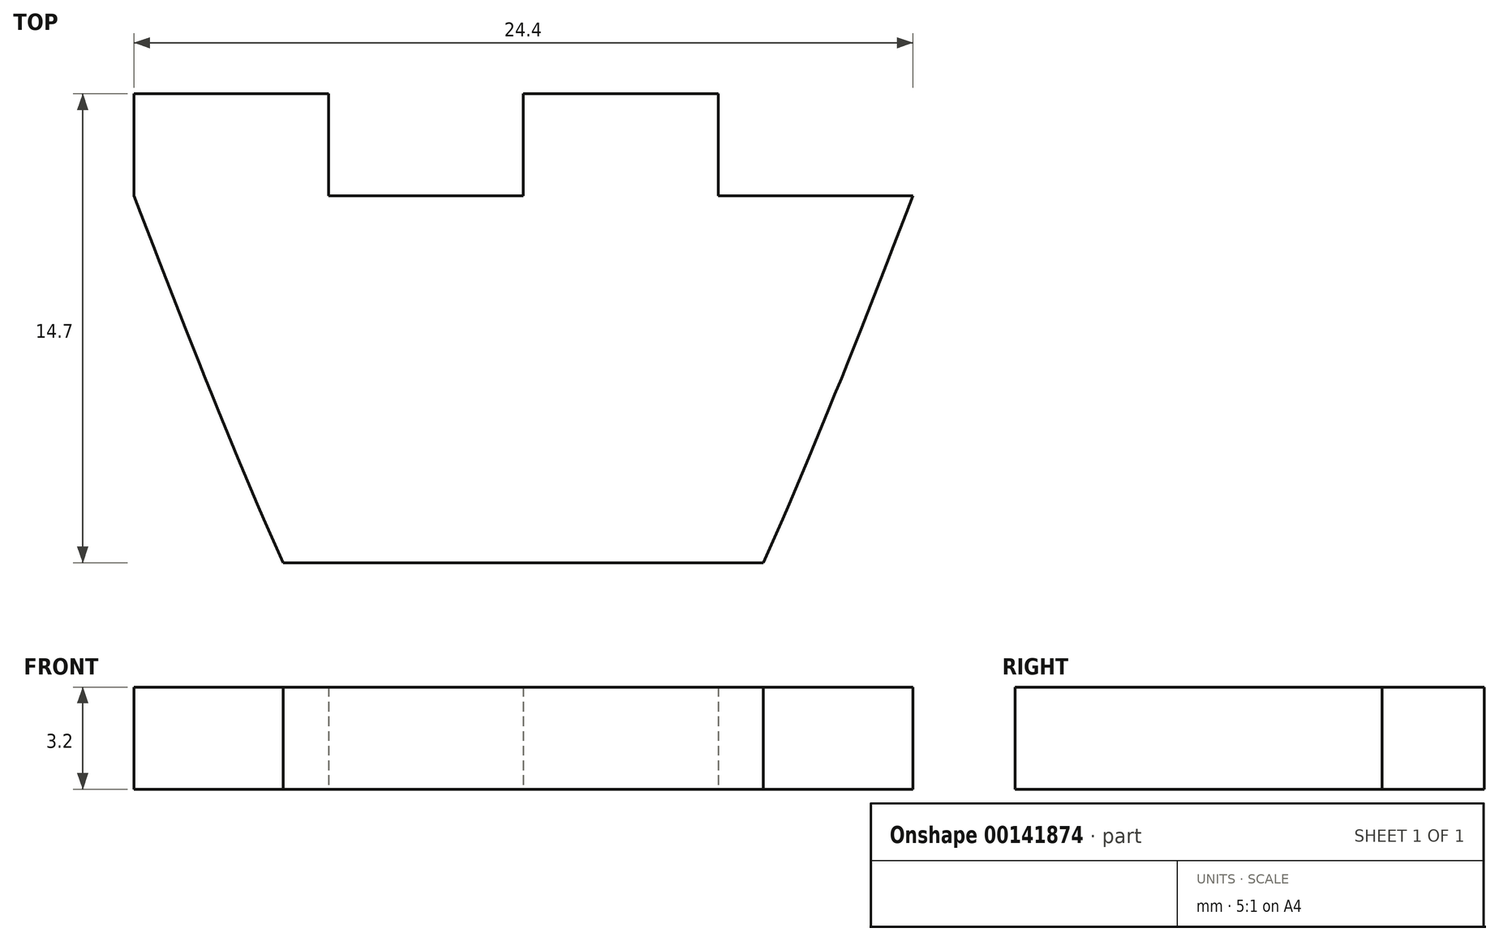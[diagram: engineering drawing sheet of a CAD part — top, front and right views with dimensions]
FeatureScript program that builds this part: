
annotation { "Feature Type Name" : "Feature", "Feature Type Description" : "" }
export const myFeature = defineFeature(function(context is Context, id is Id, definition is map)
    precondition{}
    {
        {
            var Q0;
            Q0=qCreatedBy(makeId("Top.planeOp"),FACE);
            var sketch = newSketch(context, id + "F0", { "sketchPlane" : qUnion([Q0])});
            skLineSegment(sketch, "E0", {"start": v(0, 0) * mm, "end": v(12.2, 0) * mm, "construction": true});
            skLineSegment(sketch, "E1", {"start": v(12.2, 0) * mm, "end": v(-12.2, 0) * mm, "construction": true});
            skLineSegment(sketch, "E2", {"start": v(0, 0) * mm, "end": v(0, -11.5) * mm, "construction": true});
            skFitSpline(sketch, "E3", {"points": [v(-12.2, 0) * mm, v(0, -21) * mm, v(12.2, 0) * mm], "startDerivative": vector(24.4, -63) * mm, "endDerivative": vector(24.4, 63) * mm});
            skLineSegment(sketch, "E4", {"start": v(-12.2, 0) * mm, "end": v(-12.2, 3.2) * mm});
            skLineSegment(sketch, "E5", {"start": v(-12.2, 3.2) * mm, "end": v(-6.1, 3.2) * mm});
            skLineSegment(sketch, "E6", {"start": v(-6.1, 3.2) * mm, "end": v(-6.1, 0) * mm});
            skLineSegment(sketch, "E7", {"start": v(-6.1, 0) * mm, "end": v(0, 0) * mm});
            skLineSegment(sketch, "E8", {"start": v(0, 0) * mm, "end": v(0, 3.2) * mm});
            skLineSegment(sketch, "E9", {"start": v(0, 3.2) * mm, "end": v(6.1, 3.2) * mm});
            skLineSegment(sketch, "E10", {"start": v(6.1, 3.2) * mm, "end": v(6.1, 0) * mm});
            skLineSegment(sketch, "E11", {"start": v(6.1, 0) * mm, "end": v(12.2, 0) * mm});
            skLineSegment(sketch, "E12", {"start": v(-7.52, -11.5) * mm, "end": v(7.52, -11.5) * mm});
            skSolve(sketch);
        }
        {
            var Q0;
            Q0=makeQuery(id+"F0.imprint","IMPRINT",FACE,{"disambiguationData":[TD([[makeQuery(id+"F0.imprint","IMPRINT",EDGE,{"derivedFrom":sQuery(id+"F0.wireOp",EDGE,"E3")}),1.0]])]});
            extrude(context, id + "F1", {"entities" : qUnion([Q0]), "endBound" : BoundingType.SYMMETRIC, "depth" : 3.2 * mm});
        }
    });
